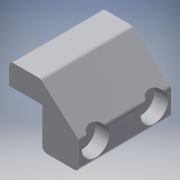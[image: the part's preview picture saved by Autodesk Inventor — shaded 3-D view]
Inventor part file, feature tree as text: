
AUTODESK INVENTOR PART (.ipt)
format: ipt  version: 2016 (Build 200138000, 138)  size: 159,232 bytes
history: native  units: in
note: dims shown in document units (in); Inventor stores cm internally (conversion verified against a paired STEP export)
features: sketch x2, extrude x1, hole x1, fillet x1
ambient origin geometry x8: Origin, YZ Plane, XZ Plane, XY Plane, X Axis, Y Axis, Z Axis, Center Point
bodies: Solid1 (feature_tree)
feature tree (5):
  extrude  "Extrusion1"  Depth=1.0in
  hole  "Hole3"  [1 undecoded]
  fillet  "Fillet2"  Radius=0.59in
  sketch  "Sketch1"  dims[d6=2.5in d7=0.0in d39=1.0in]
  sketch  "Sketch5"  dims[d40=0.905in d42=1.09in d43=0.59in d45=0.3324in d46=0.75in d47=0.5in d48=0.45in d49=0.266in d50=0.75in d51=0.75in d52=0.375in d53=0.5635in d54=1.0in d55=0.8108in d56=0.125in]
note: 1 required parameter value undecoded (feature->parameter linkage not recoverable at this tier; creation-order binding heuristic only, values carry confidence <= 0.55)
